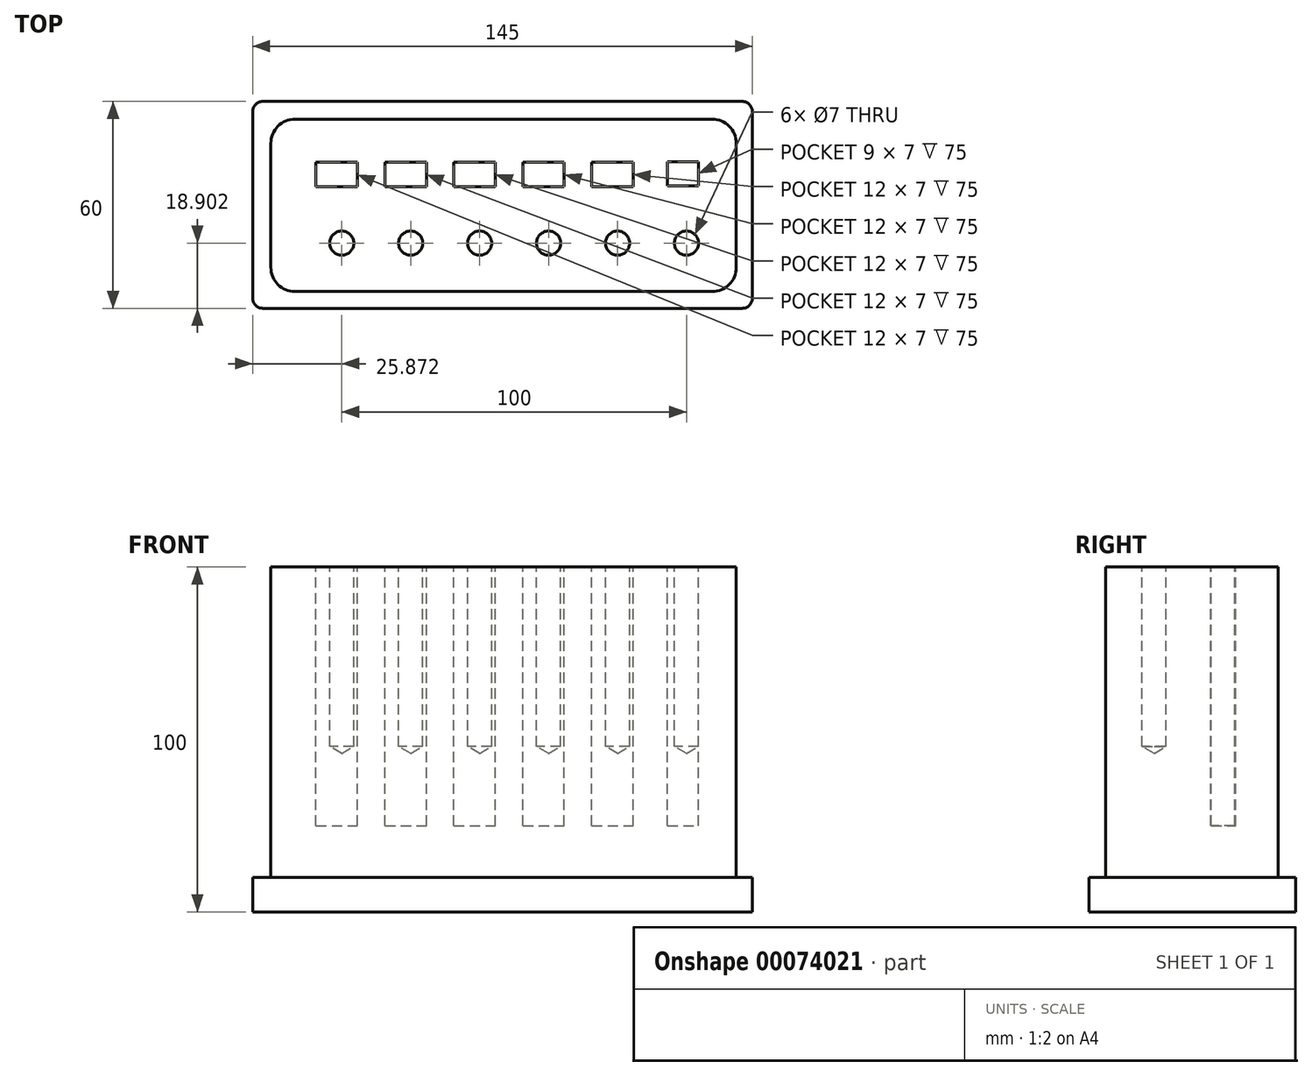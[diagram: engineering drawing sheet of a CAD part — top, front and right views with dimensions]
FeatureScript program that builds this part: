
annotation { "Feature Type Name" : "Feature", "Feature Type Description" : "" }
export const myFeature = defineFeature(function(context is Context, id is Id, definition is map)
    precondition{}
    {
        {
            var Q0;
            Q0=qCreatedBy(makeId("Front.planeOp"),FACE);
            var sketch = newSketch(context, id + "F0", { "sketchPlane" : qUnion([Q0])});
            skLineSegment(sketch, "E0.bottom", {"start": v(0, 0) * mm, "end": v(135, 0) * mm});
            skLineSegment(sketch, "E0.top", {"start": v(0, 100) * mm, "end": v(135, 100) * mm});
            skLineSegment(sketch, "E0.left", {"start": v(0, 0) * mm, "end": v(0, 100) * mm});
            skLineSegment(sketch, "E0.right", {"start": v(135, 0) * mm, "end": v(135, 100) * mm});
            skSolve(sketch);
        }
        {
            var Q0;
            Q0=makeQuery(id+"F0.imprint","IMPRINT",FACE,{"disambiguationData":[TD([[makeQuery(id+"F0.imprint","IMPRINT",EDGE,{"derivedFrom":sQuery(id+"F0.wireOp",EDGE,"E0.bottom")}),1.0]])]});
            extrude(context, id + "F1", {"entities" : qUnion([Q0]), "depth" : 50 * mm});
        }
        {
            var Q0;
            Q0=makeQuery(id+"F1.opExtrude","SWEPT_FACE",FACE,{"disambiguationData":[OSD([sQuery(id+"F0.wireOp",EDGE,"E0.top")])]});
            var sketch = newSketch(context, id + "F2", { "sketchPlane" : qUnion([Q0])});
            skLineSegment(sketch, "E1.bottom", {"start": v(13.12, -12.53) * mm, "end": v(25.12, -12.53) * mm});
            skLineSegment(sketch, "E1.top", {"start": v(13.12, -19.53) * mm, "end": v(25.12, -19.53) * mm});
            skLineSegment(sketch, "E1.left", {"start": v(13.12, -12.53) * mm, "end": v(13.12, -19.53) * mm});
            skLineSegment(sketch, "E1.right", {"start": v(25.12, -12.53) * mm, "end": v(25.12, -19.53) * mm});
            skLineSegment(sketch, "E2.1.0.0", {"start": v(33.12, -12.53) * mm, "end": v(45.12, -12.53) * mm});
            skLineSegment(sketch, "E2.1.0.1", {"start": v(33.12, -19.53) * mm, "end": v(45.12, -19.53) * mm});
            skLineSegment(sketch, "E2.1.0.2", {"start": v(33.12, -12.53) * mm, "end": v(33.12, -19.53) * mm});
            skLineSegment(sketch, "E2.1.0.3", {"start": v(45.12, -12.53) * mm, "end": v(45.12, -19.53) * mm});
            skLineSegment(sketch, "E2.2.0.0", {"start": v(53.12, -12.53) * mm, "end": v(65.12, -12.53) * mm});
            skLineSegment(sketch, "E2.2.0.1", {"start": v(53.12, -19.53) * mm, "end": v(65.12, -19.53) * mm});
            skLineSegment(sketch, "E2.2.0.2", {"start": v(53.12, -12.53) * mm, "end": v(53.12, -19.53) * mm});
            skLineSegment(sketch, "E2.2.0.3", {"start": v(65.12, -12.53) * mm, "end": v(65.12, -19.53) * mm});
            skLineSegment(sketch, "E2.3.0.0", {"start": v(73.12, -12.53) * mm, "end": v(85.12, -12.53) * mm});
            skLineSegment(sketch, "E2.3.0.1", {"start": v(73.12, -19.53) * mm, "end": v(85.12, -19.53) * mm});
            skLineSegment(sketch, "E2.3.0.2", {"start": v(73.12, -12.53) * mm, "end": v(73.12, -19.53) * mm});
            skLineSegment(sketch, "E2.3.0.3", {"start": v(85.12, -12.53) * mm, "end": v(85.12, -19.53) * mm});
            skLineSegment(sketch, "E2.4.0.0", {"start": v(93.12, -12.53) * mm, "end": v(105.12, -12.53) * mm});
            skLineSegment(sketch, "E2.4.0.1", {"start": v(93.12, -19.53) * mm, "end": v(105.12, -19.53) * mm});
            skLineSegment(sketch, "E2.4.0.2", {"start": v(93.12, -12.53) * mm, "end": v(93.12, -19.53) * mm});
            skLineSegment(sketch, "E2.4.0.3", {"start": v(105.12, -12.53) * mm, "end": v(105.12, -19.53) * mm});
            skLineSegment(sketch, "E3.bottom", {"start": v(115.09, -19.33) * mm, "end": v(124.09, -19.33) * mm});
            skLineSegment(sketch, "E3.top", {"start": v(115.09, -12.33) * mm, "end": v(124.09, -12.33) * mm});
            skLineSegment(sketch, "E3.left", {"start": v(115.09, -19.33) * mm, "end": v(115.09, -12.33) * mm});
            skLineSegment(sketch, "E3.right", {"start": v(124.09, -19.33) * mm, "end": v(124.09, -12.33) * mm});
            skSolve(sketch);
        }
        {
            var Q0;
            Q0 = qSketchRegion(id + "F2", true);
            extrude(context, id + "F3", {"entities" : qUnion([Q0]), "operationType" : NewBodyOperationType.REMOVE, "oppositeDirection" : true, "depth" : 75 * mm});
        }
        {
            var Q0;
            Q0=makeQuery(id+"F1.opExtrude","SWEPT_FACE",FACE,{"disambiguationData":[OSD([sQuery(id+"F0.wireOp",EDGE,"E0.top")])]});
            var sketch = newSketch(context, id + "F4", { "sketchPlane" : qUnion([Q0])});
            skPoint(sketch, "E4", {"position": v(20.57, -35.95) * mm});
            skPoint(sketch, "E5.1.0.0", {"position": v(40.57, -35.95) * mm});
            skPoint(sketch, "E5.2.0.0", {"position": v(60.57, -35.95) * mm});
            skPoint(sketch, "E5.3.0.0", {"position": v(80.57, -35.95) * mm});
            skPoint(sketch, "E5.4.0.0", {"position": v(100.57, -35.95) * mm});
            skPoint(sketch, "E5.5.0.0", {"position": v(120.57, -35.95) * mm});
            skSolve(sketch);
        }
        {
            var Q0;
            Q0=sQuery(id+"F4.wireOp",VERTEX,"E4");
            var Q1;
            Q1=sQuery(id+"F4.wireOp",VERTEX,"E5.1.0.0");
            var Q2;
            Q2=sQuery(id+"F4.wireOp",VERTEX,"E5.2.0.0");
            var Q3;
            Q3=sQuery(id+"F4.wireOp",VERTEX,"E5.3.0.0");
            var Q4;
            Q4=sQuery(id+"F4.wireOp",VERTEX,"E5.4.0.0");
            var Q5;
            Q5=sQuery(id+"F4.wireOp",VERTEX,"E5.5.0.0");
            var Q6;
            Q6=sQuery(id+"F4.wireOp",VERTEX,"9d9bda47-70df-447a-b46a-f549a8aedada");
            var Q7;
            Q7=sQuery(id+"F4.wireOp",VERTEX,"98971a5a-94c1-4367-8f6a-343a0bd0424e.1.0.0");
            var Q8;
            Q8=sQuery(id+"F4.wireOp",VERTEX,"98971a5a-94c1-4367-8f6a-343a0bd0424e.2.0.0");
            var Q9;
            Q9=sQuery(id+"F4.wireOp",VERTEX,"98971a5a-94c1-4367-8f6a-343a0bd0424e.3.0.0");
            var Q10;
            Q10=sQuery(id+"F4.wireOp",VERTEX,"98971a5a-94c1-4367-8f6a-343a0bd0424e.4.0.0");
            var Q11;
            Q11=sQuery(id+"F4.wireOp",VERTEX,"98971a5a-94c1-4367-8f6a-343a0bd0424e.5.0.0");
            var Q12;
            Q12=makeQuery(id+"F1.opExtrude","SWEPT_BODY",BODY,{"disambiguationData":[OSD([sQuery(id+"F0.wireOp",EDGE,"E0.bottom"),sQuery(id+"F0.wireOp",EDGE,"E0.top"),sQuery(id+"F0.wireOp",EDGE,"E0.left"),sQuery(id+"F0.wireOp",EDGE,"E0.right")])]});
            hole(context, id + "F5", {"style" : HoleStyle.SIMPLE, "endStyle" : HoleEndStyle.BLIND, "holeDiameter" : 7 * mm, "holeDepth" : 52 * mm, "tappedDepth" : 12 * mm, "tapClearance" : 3, "locations" : qUnion([Q0, Q1, Q2, Q3, Q4, Q5, Q6, Q7, Q8, Q9, Q10, Q11]), "scope" : qUnion([Q12])});
        }
        {
            var Q0;
            Q0=qCreatedBy(makeId("Top.planeOp"),FACE);
            var sketch = newSketch(context, id + "F6", { "sketchPlane" : qUnion([Q0])});
            skLineSegment(sketch, "E6.bottom", {"start": v(-5.3, 5.15) * mm, "end": v(139.7, 5.15) * mm});
            skLineSegment(sketch, "E6.top", {"start": v(-5.3, -54.85) * mm, "end": v(139.7, -54.85) * mm});
            skLineSegment(sketch, "E6.left", {"start": v(-5.3, 5.15) * mm, "end": v(-5.3, -54.85) * mm});
            skLineSegment(sketch, "E6.right", {"start": v(139.7, 5.15) * mm, "end": v(139.7, -54.85) * mm});
            skSolve(sketch);
        }
        {
            var Q0;
            Q0=makeQuery(id+"F6.imprint","IMPRINT",FACE,{"disambiguationData":[TD([[makeQuery(id+"F6.imprint","IMPRINT",EDGE,{"derivedFrom":sQuery(id+"F6.wireOp",EDGE,"E6.bottom")}),-1.0]])]});
            extrude(context, id + "F7", {"entities" : qUnion([Q0]), "operationType" : NewBodyOperationType.ADD, "depth" : 10 * mm});
        }
        {
            var Q0;
            Q0=makeQuery(id+"F1.opExtrude","CAP_EDGE",EDGE,{"disambiguationData":[OSD([sQuery(id+"F0.wireOp",EDGE,"E0.left")])],"isStart":false});
            var Q1;
            Q1=makeQuery(id+"F1.opExtrude","CAP_EDGE",EDGE,{"disambiguationData":[OSD([sQuery(id+"F0.wireOp",EDGE,"E0.right")])],"isStart":false});
            var Q2;
            Q2=makeQuery(id+"F1.opExtrude","CAP_EDGE",EDGE,{"disambiguationData":[OSD([sQuery(id+"F0.wireOp",EDGE,"E0.right")])],"isStart":true});
            var Q3;
            Q3=makeQuery(id+"F1.opExtrude","CAP_EDGE",EDGE,{"disambiguationData":[OSD([sQuery(id+"F0.wireOp",EDGE,"E0.left")])],"isStart":true});
            fillet(context, id + "F8", {"entities" : qUnion([Q0, Q1, Q2, Q3]), "radius" : 7 * mm, "tangentPropagation" : true, "allowEdgeOverflow" : false});
        }
        {
            var Q0;
            Q0=makeQuery(id+"F7.opExtrude","SWEPT_EDGE",EDGE,{"disambiguationData":[OSD([sQuery(id+"F6.wireOp",EDGE,"E6.bottom"),sQuery(id+"F6.wireOp",EDGE,"E6.left")])]});
            var Q1;
            Q1=makeQuery(id+"F7.opExtrude","SWEPT_EDGE",EDGE,{"disambiguationData":[OSD([sQuery(id+"F6.wireOp",EDGE,"E6.top"),sQuery(id+"F6.wireOp",EDGE,"E6.left")])]});
            var Q2;
            Q2=makeQuery(id+"F7.opExtrude","SWEPT_EDGE",EDGE,{"disambiguationData":[OSD([sQuery(id+"F6.wireOp",EDGE,"E6.top"),sQuery(id+"F6.wireOp",EDGE,"E6.right")])]});
            var Q3;
            Q3=makeQuery(id+"F7.opExtrude","SWEPT_EDGE",EDGE,{"disambiguationData":[OSD([sQuery(id+"F6.wireOp",EDGE,"E6.bottom"),sQuery(id+"F6.wireOp",EDGE,"E6.right")])]});
            fillet(context, id + "F9", {"entities" : qUnion([Q0, Q1, Q2, Q3]), "radius" : 3 * mm, "tangentPropagation" : true, "allowEdgeOverflow" : false});
        }
    });
